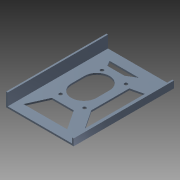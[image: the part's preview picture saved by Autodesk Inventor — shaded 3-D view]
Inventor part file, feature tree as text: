
AUTODESK INVENTOR PART (.ipt)
format: ipt  version: 2013 (Build 170138000, 138)  size: 167,936 bytes
history: native  units: mm
features: sketch x5, extrude x4, other x1, hole x1
ambient origin geometry x1: Origin
feature tree (11):
  other  "ソリッド1"
  extrude  "押し出し1"  Depth=92.0mm
  hole  "穴1"  [1 undecoded]
  extrude  "押し出し3"  Depth=62.0mm
  extrude  "押し出し5"  Depth=31.0mm
  extrude  "押し出し6"  Depth=1.5mm TaperAngle=0.0deg
  sketch  "スケッチ1"
  sketch  "スケッチ3"
  sketch  "スケッチ4"
  sketch  "スケッチ6"
  sketch  "スケッチ7"
note: 1 required parameter value undecoded (feature->parameter linkage not recoverable at this tier; creation-order binding heuristic only, values carry confidence <= 0.55)
